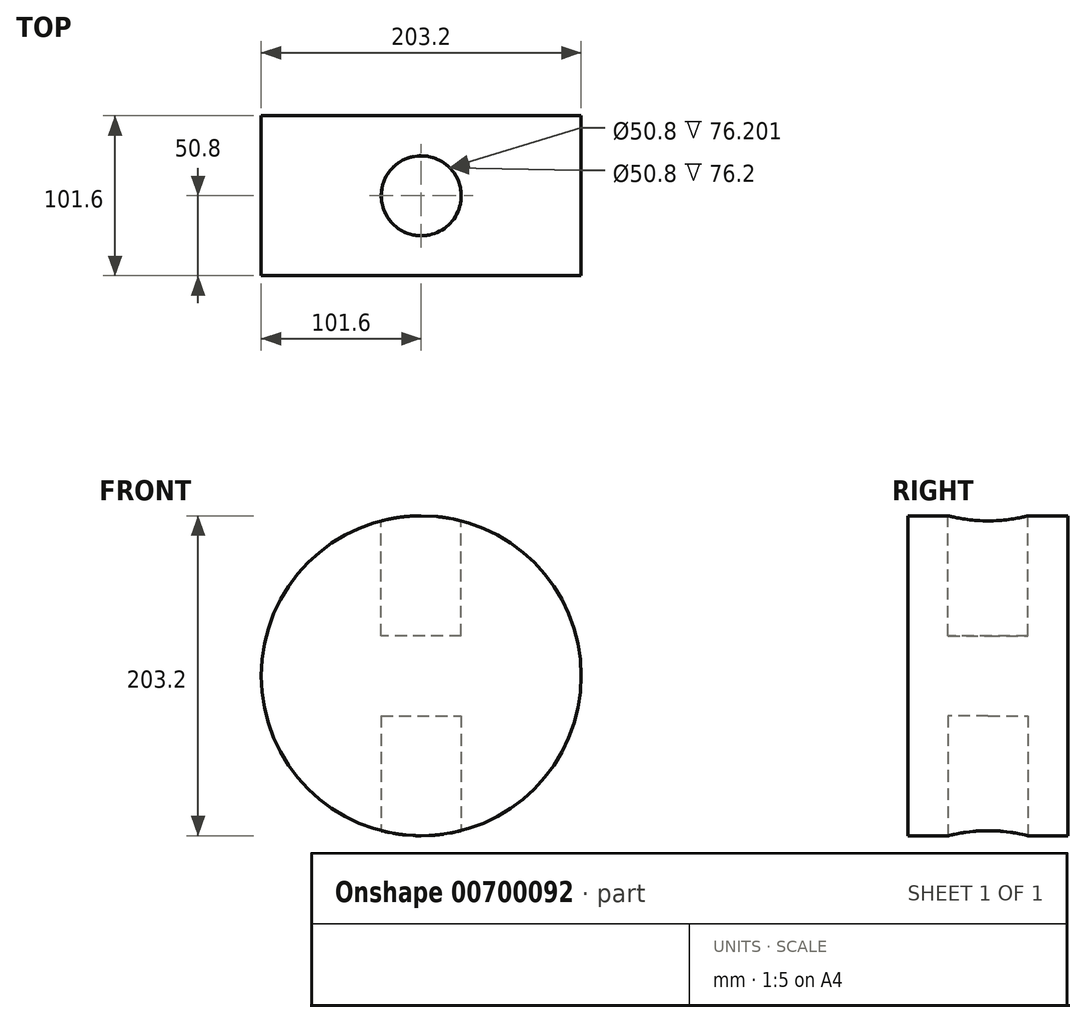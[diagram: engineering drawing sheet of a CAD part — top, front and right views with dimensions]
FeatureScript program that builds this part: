
annotation { "Feature Type Name" : "Feature", "Feature Type Description" : "" }
export const myFeature = defineFeature(function(context is Context, id is Id, definition is map)
    precondition{}
    {
        {
            var Q0;
            Q0=qCreatedBy(makeId("Front.planeOp"),FACE);
            var sketch = newSketch(context, id + "F0", { "sketchPlane" : qUnion([Q0])});
            skCircle(sketch, "E0", {"center": v(0, 0) * mm, "radius": 101.6 * mm});
            skSolve(sketch);
        }
        {
            var Q0;
            Q0 = qSketchRegion(id + "F0", true);
            extrude(context, id + "F1", {"entities" : qUnion([Q0]), "depth" : 101.6 * mm, "offsetDistance" : 25.4 * mm});
        }
        {
            var Q0;
            Q0=qCreatedBy(makeId("Top.planeOp"),FACE);
            cPlane(context, id + "F2", {"entities" : qUnion([Q0]), "cplaneType" : CPlaneType.OFFSET, "offset" : 101.6 * mm, "width" : 152.4 * mm, "height" : 152.4 * mm});
        }
        {
            var Q0;
            Q0=qCreatedBy(id+"F2.planeOp",FACE);
            var sketch = newSketch(context, id + "F3", { "sketchPlane" : qUnion([Q0])});
            skCircle(sketch, "E1", {"center": v(0, -50.8) * mm, "radius": 25.4 * mm});
            skSolve(sketch);
        }
        {
            var Q0;
            Q0 = qSketchRegion(id + "F3", true);
            extrude(context, id + "F4", {"entities" : qUnion([Q0]), "operationType" : NewBodyOperationType.REMOVE, "oppositeDirection" : true, "depth" : 76.2 * mm, "offsetDistance" : 25.4 * mm});
        }
        {
            var Q0;
            Q0=qCreatedBy(makeId("Top.planeOp"),FACE);
            cPlane(context, id + "F5", {"entities" : qUnion([Q0]), "cplaneType" : CPlaneType.OFFSET, "offset" : 101.6 * mm, "oppositeDirection" : true, "width" : 152.4 * mm, "height" : 152.4 * mm});
        }
        {
            var Q0;
            Q0=qCreatedBy(id+"F5.planeOp",FACE);
            var sketch = newSketch(context, id + "F6", { "sketchPlane" : qUnion([Q0])});
            skCircle(sketch, "E2", {"center": v(0, -50.8) * mm, "radius": 25.4 * mm});
            skSolve(sketch);
        }
        {
            var Q0;
            Q0 = qSketchRegion(id + "F6", true);
            extrude(context, id + "F7", {"entities" : qUnion([Q0]), "operationType" : NewBodyOperationType.REMOVE, "depth" : 76.2 * mm, "offsetDistance" : 25.4 * mm});
        }
    });
